# Revit family: Faucet-Utility-KOHLER-Triton-K-7319_1
name_source: partatom
category: Plumbing Fixtures
revit_build: Autodesk Revit 2017 (Build: 20160225_1515(x64)
units: mm (PartAtom-declared; Revit-internal decimal feet)

## family parameters
Cut with Voids When Loaded = No
Host = Face
OmniClass Number = 23.31.11.00
OmniClass Title = Faucets
Part Type = Normal
Room Calculation Point = No
Round Connector Dimension = Use Diameter
Shared = No

## types (2) — shared parameters
ADA Compliant = Yes
Assembly Code = D2010
CW Connection = Yes
Cold Water Inlet = Cold Water Inlet
Date Modified = 08/16/2021
Default Elevation = 36"
Drain Included = No
Faucet Hole Spacing = 8 1/16"
Finish = Kohler-Metal-CP-Polished_Chrome
Flow Rate = 2 GPM
HW Connection = Yes
Height = 12 11/16"
Hot Water Inlet = Hot Water Inlet
Length = 8 5/16"
Manufacturer = KOHLER Co.
Master Format 2014 = 22 41 39
Master Format 2014 Name = Residential Faucets, Supplies, and Trim
Material = Brass Construction
Pressure = 60.00 psi
Product Documentation Link = https://www.us.kohler.com
Product Name = Triton
Product Page URL = http://www.us.kohler.com
Spout Reach = 5 3/16"
URL = https://www.us.kohler.com
Vent Connection = No
Waste Connection = No
Waste Water Outlet = Waste Water Outlet
WaterSense Certified = No
Width = 8 1/16"

## per-type parameters (varying)
| type | Cross Handle | Description | Handle Clearance | Lever Handle | Model | Type |
| Cross Handle, CP-Polished Chrome | Yes | Double cross handle utility sink faucet with rosespray gooseneck spout | 1 3/16" | No | K-7319-3-CP | 1 |
| Lever Handle, CP-Polished Chrome | No | Double lever handle utility sink faucet with rosespray gooseneck spout | 1 15/16" | Yes | K-7319-4-CP | 2 |

## geometry (parser evidence)
native form markers: Sweep x4
no freeform markers — native parametric forms only
